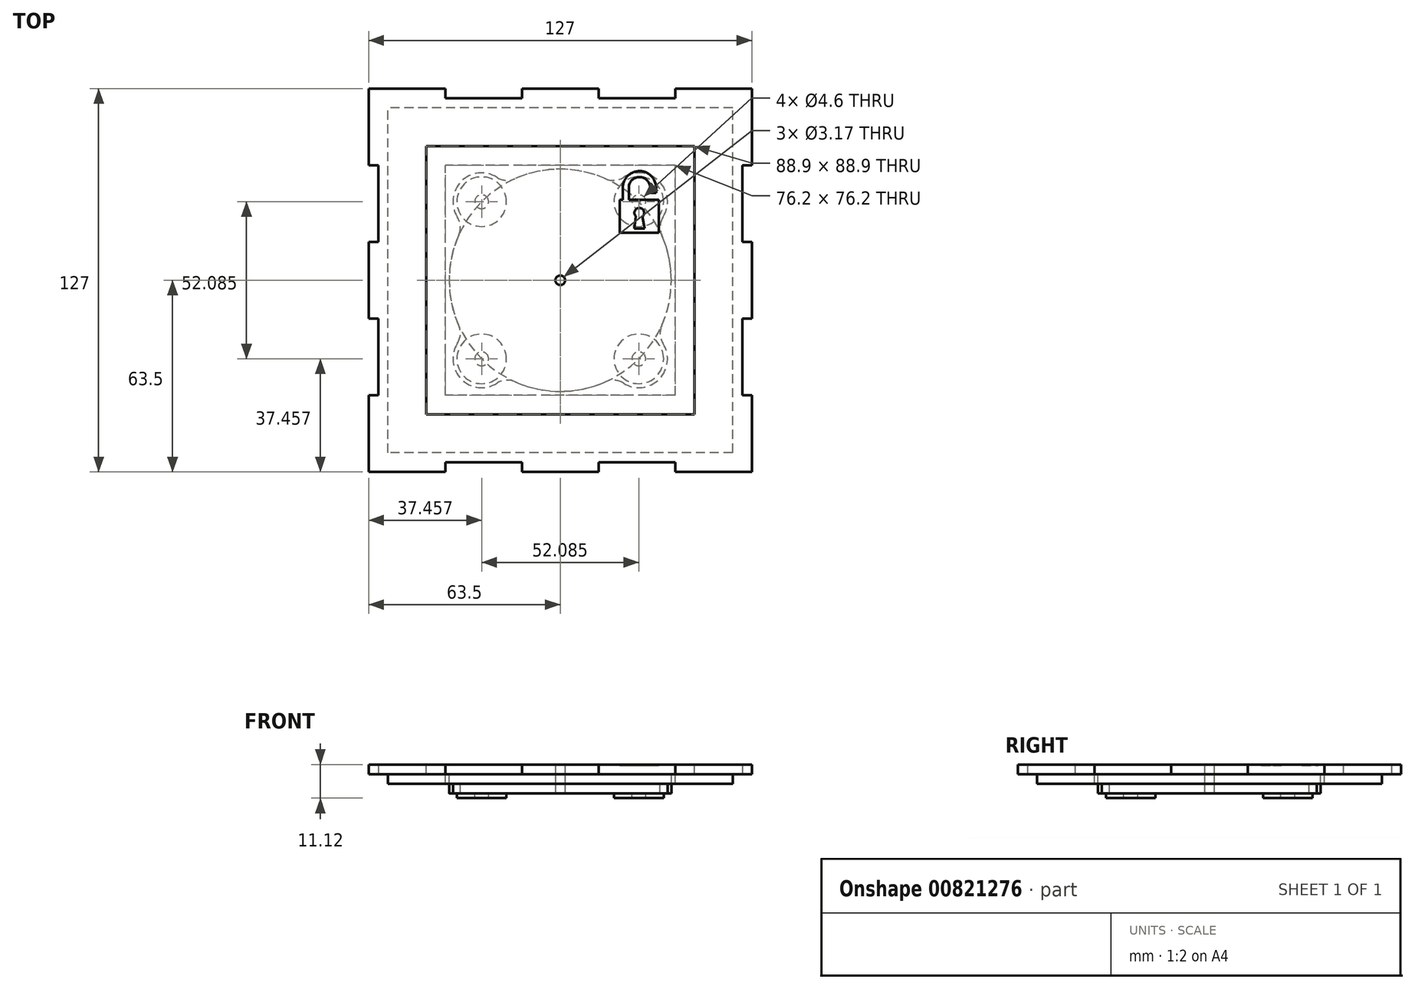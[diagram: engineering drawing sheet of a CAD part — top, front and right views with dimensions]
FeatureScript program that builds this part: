
annotation { "Feature Type Name" : "Feature", "Feature Type Description" : "" }
export const myFeature = defineFeature(function(context is Context, id is Id, definition is map)
    precondition{}
    {
        {
            var Q0;
            Q0=qCreatedBy(makeId("Top.planeOp"),FACE);
            var sketch = newSketch(context, id + "F0", { "sketchPlane" : qUnion([Q0])});
            skLineSegment(sketch, "E0.bottom", {"start": v(-63.5, 63.5) * mm, "end": v(63.5, 63.5) * mm});
            skLineSegment(sketch, "E0.top", {"start": v(-63.5, -63.5) * mm, "end": v(63.5, -63.5) * mm});
            skLineSegment(sketch, "E0.left", {"start": v(-63.5, 63.5) * mm, "end": v(-63.5, -63.5) * mm});
            skLineSegment(sketch, "E0.right", {"start": v(63.5, 63.5) * mm, "end": v(63.5, -63.5) * mm});
            skPoint(sketch, "E0.middle", {"position": v(0, 0) * mm});
            skLineSegment(sketch, "E1", {"start": v(-38.1, 63.5) * mm, "end": v(-38.1, -63.5) * mm});
            skLineSegment(sketch, "E2", {"start": v(-63.5, -38.1) * mm, "end": v(63.5, -38.1) * mm});
            skLineSegment(sketch, "E3.1.0.0", {"start": v(-12.7, 63.5) * mm, "end": v(-12.7, -63.5) * mm});
            skLineSegment(sketch, "E3.2.0.0", {"start": v(12.7, 63.5) * mm, "end": v(12.7, -63.5) * mm});
            skLineSegment(sketch, "E3.3.0.0", {"start": v(38.1, 63.5) * mm, "end": v(38.1, -63.5) * mm});
            skLineSegment(sketch, "E3.direction1", {"start": v(-38.1, -63.5) * mm, "end": v(-12.7, -63.5) * mm, "construction": true});
            skLineSegment(sketch, "E4.0.1.0", {"start": v(-63.5, -12.7) * mm, "end": v(63.5, -12.7) * mm});
            skLineSegment(sketch, "E4.0.2.0", {"start": v(-63.5, 12.7) * mm, "end": v(63.5, 12.7) * mm});
            skLineSegment(sketch, "E4.0.3.0", {"start": v(-63.5, 38.1) * mm, "end": v(63.5, 38.1) * mm});
            skLineSegment(sketch, "E4.1.0.0", {"start": v(-38.1, -38.1) * mm, "end": v(63.5, -38.1) * mm});
            skLineSegment(sketch, "E4.1.1.0", {"start": v(-38.1, -12.7) * mm, "end": v(63.5, -12.7) * mm});
            skLineSegment(sketch, "E4.1.2.0", {"start": v(-38.1, 12.7) * mm, "end": v(63.5, 12.7) * mm});
            skLineSegment(sketch, "E4.1.3.0", {"start": v(-38.1, 38.1) * mm, "end": v(63.5, 38.1) * mm});
            skLineSegment(sketch, "E4.2.0.0", {"start": v(-12.7, -38.1) * mm, "end": v(63.5, -38.1) * mm});
            skLineSegment(sketch, "E4.2.1.0", {"start": v(-12.7, -12.7) * mm, "end": v(63.5, -12.7) * mm});
            skLineSegment(sketch, "E4.2.2.0", {"start": v(-12.7, 12.7) * mm, "end": v(63.5, 12.7) * mm});
            skLineSegment(sketch, "E4.2.3.0", {"start": v(-12.7, 38.1) * mm, "end": v(63.5, 38.1) * mm});
            skLineSegment(sketch, "E4.direction1", {"start": v(-63.5, -38.1) * mm, "end": v(-38.1, -38.1) * mm, "construction": true});
            skLineSegment(sketch, "E4.direction2", {"start": v(-63.5, -38.1) * mm, "end": v(-63.5, -12.7) * mm, "construction": true});
            skLineSegment(sketch, "E5", {"start": v(-63.5, -60.33) * mm, "end": v(63.5, -60.32) * mm});
            skLineSegment(sketch, "E6", {"start": v(-60.33, 63.5) * mm, "end": v(-60.33, -63.5) * mm});
            skLineSegment(sketch, "E7", {"start": v(-63.5, 60.33) * mm, "end": v(63.5, 60.33) * mm});
            skLineSegment(sketch, "E8", {"start": v(60.32, 63.5) * mm, "end": v(60.32, -63.5) * mm});
            skSolve(sketch);
        }
        {
            var Q0;
            {var subQ0=sQuery(id+"F0.wireOp",EDGE,"E6");var subQ1=sQuery(id+"F0.wireOp",EDGE,"E0.bottom");var subQ2=makeQuery(id+"F0.imprint","INTERSECT",VERTEX,{"derivedFrom":[subQ1,subQ0]});Q0=makeQuery(id+"F0.imprint","IMPRINT",FACE,{"disambiguationData":[TD([[makeQuery(id+"F0.imprint","IMPRINT",EDGE,{"disambiguationData":[TD([[subQ2,1.0]])],"derivedFrom":subQ1}),-1.0]])]});}
            var Q1;
            {var subQ0=sQuery(id+"F0.wireOp",EDGE,"E0.right");var subQ1=sQuery(id+"F0.wireOp",EDGE,"E0.bottom");var subQ2=makeQuery(id+"F0.imprint","INTERSECT",VERTEX,{"derivedFrom":[subQ1,subQ0]});Q1=makeQuery(id+"F0.imprint","IMPRINT",FACE,{"disambiguationData":[TD([[makeQuery(id+"F0.imprint","IMPRINT",EDGE,{"disambiguationData":[TD([[subQ2,1.0]])],"derivedFrom":subQ1}),-1.0]])]});}
            var Q2;
            {var subQ0=sQuery(id+"F0.wireOp",EDGE,"E6");var subQ1=sQuery(id+"F0.wireOp",EDGE,"E0.top");var subQ2=makeQuery(id+"F0.imprint","INTERSECT",VERTEX,{"derivedFrom":[subQ1,subQ0]});Q2=makeQuery(id+"F0.imprint","IMPRINT",FACE,{"disambiguationData":[TD([[makeQuery(id+"F0.imprint","IMPRINT",EDGE,{"disambiguationData":[TD([[subQ2,1.0]])],"derivedFrom":subQ1}),1.0]])]});}
            var Q3;
            {var subQ0=sQuery(id+"F0.wireOp",EDGE,"E0.right");var subQ1=sQuery(id+"F0.wireOp",EDGE,"E0.top");var subQ2=makeQuery(id+"F0.imprint","INTERSECT",VERTEX,{"derivedFrom":[subQ1,subQ0]});Q3=makeQuery(id+"F0.imprint","IMPRINT",FACE,{"disambiguationData":[TD([[makeQuery(id+"F0.imprint","IMPRINT",EDGE,{"disambiguationData":[TD([[subQ2,1.0]])],"derivedFrom":subQ1}),1.0]])]});}
            var Q4;
            {var subQ0=sQuery(id+"F0.wireOp",EDGE,"E1");var subQ1=sQuery(id+"F0.wireOp",EDGE,"E0.bottom");var subQ2=makeQuery(id+"F0.imprint","INTERSECT",VERTEX,{"derivedFrom":[subQ1,subQ0]});Q4=makeQuery(id+"F0.imprint","IMPRINT",FACE,{"disambiguationData":[TD([[makeQuery(id+"F0.imprint","IMPRINT",EDGE,{"disambiguationData":[TD([[subQ2,1.0]])],"derivedFrom":subQ1}),-1.0]])]});}
            var Q5;
            {var subQ0=sQuery(id+"F0.wireOp",EDGE,"E3.1.0.0");var subQ1=sQuery(id+"F0.wireOp",EDGE,"E0.bottom");var subQ2=makeQuery(id+"F0.imprint","INTERSECT",VERTEX,{"derivedFrom":[subQ1,subQ0]});Q5=makeQuery(id+"F0.imprint","IMPRINT",FACE,{"disambiguationData":[TD([[makeQuery(id+"F0.imprint","IMPRINT",EDGE,{"disambiguationData":[TD([[subQ2,-1.0]])],"derivedFrom":subQ1}),-1.0]])]});}
            var Q6;
            {var subQ0=sQuery(id+"F0.wireOp",EDGE,"E3.3.0.0");var subQ1=sQuery(id+"F0.wireOp",EDGE,"E0.bottom");var subQ2=makeQuery(id+"F0.imprint","INTERSECT",VERTEX,{"derivedFrom":[subQ1,subQ0]});Q6=makeQuery(id+"F0.imprint","IMPRINT",FACE,{"disambiguationData":[TD([[makeQuery(id+"F0.imprint","IMPRINT",EDGE,{"disambiguationData":[TD([[subQ2,-1.0]])],"derivedFrom":subQ1}),-1.0]])]});}
            var Q7;
            {var subQ0=sQuery(id+"F0.wireOp",EDGE,"E1");var subQ1=sQuery(id+"F0.wireOp",EDGE,"E0.top");var subQ2=makeQuery(id+"F0.imprint","INTERSECT",VERTEX,{"derivedFrom":[subQ1,subQ0]});Q7=makeQuery(id+"F0.imprint","IMPRINT",FACE,{"disambiguationData":[TD([[makeQuery(id+"F0.imprint","IMPRINT",EDGE,{"disambiguationData":[TD([[subQ2,1.0]])],"derivedFrom":subQ1}),1.0]])]});}
            var Q8;
            {var subQ0=sQuery(id+"F0.wireOp",EDGE,"E3.1.0.0");var subQ1=sQuery(id+"F0.wireOp",EDGE,"E0.top");var subQ2=makeQuery(id+"F0.imprint","INTERSECT",VERTEX,{"derivedFrom":[subQ1,subQ0]});Q8=makeQuery(id+"F0.imprint","IMPRINT",FACE,{"disambiguationData":[TD([[makeQuery(id+"F0.imprint","IMPRINT",EDGE,{"disambiguationData":[TD([[subQ2,-1.0]])],"derivedFrom":subQ1}),1.0]])]});}
            var Q9;
            {var subQ0=sQuery(id+"F0.wireOp",EDGE,"E3.3.0.0");var subQ1=sQuery(id+"F0.wireOp",EDGE,"E0.top");var subQ2=makeQuery(id+"F0.imprint","INTERSECT",VERTEX,{"derivedFrom":[subQ1,subQ0]});Q9=makeQuery(id+"F0.imprint","IMPRINT",FACE,{"disambiguationData":[TD([[makeQuery(id+"F0.imprint","IMPRINT",EDGE,{"disambiguationData":[TD([[subQ2,-1.0]])],"derivedFrom":subQ1}),1.0]])]});}
            var Q10;
            {var subQ0=sQuery(id+"F0.wireOp",EDGE,"E7");var subQ1=sQuery(id+"F0.wireOp",EDGE,"E0.left");var subQ2=makeQuery(id+"F0.imprint","INTERSECT",VERTEX,{"derivedFrom":[subQ1,subQ0]});Q10=makeQuery(id+"F0.imprint","IMPRINT",FACE,{"disambiguationData":[TD([[makeQuery(id+"F0.imprint","IMPRINT",EDGE,{"disambiguationData":[TD([[subQ2,-1.0]])],"derivedFrom":subQ1}),1.0]])]});}
            var Q11;
            {var subQ0=sQuery(id+"F0.wireOp",EDGE,"E4.0.2.0");var subQ1=sQuery(id+"F0.wireOp",EDGE,"E0.left");var subQ2=makeQuery(id+"F0.imprint","INTERSECT",VERTEX,{"derivedFrom":[subQ1,subQ0]});Q11=makeQuery(id+"F0.imprint","IMPRINT",FACE,{"disambiguationData":[TD([[makeQuery(id+"F0.imprint","IMPRINT",EDGE,{"disambiguationData":[TD([[subQ2,-1.0]])],"derivedFrom":subQ1}),1.0]])]});}
            var Q12;
            {var subQ0=sQuery(id+"F0.wireOp",EDGE,"E2");var subQ1=sQuery(id+"F0.wireOp",EDGE,"E0.left");var subQ2=makeQuery(id+"F0.imprint","INTERSECT",VERTEX,{"derivedFrom":[subQ1,subQ0]});Q12=makeQuery(id+"F0.imprint","IMPRINT",FACE,{"disambiguationData":[TD([[makeQuery(id+"F0.imprint","IMPRINT",EDGE,{"disambiguationData":[TD([[subQ2,-1.0]])],"derivedFrom":subQ1}),1.0]])]});}
            var Q13;
            {var subQ0=sQuery(id+"F0.wireOp",EDGE,"E7");var subQ1=sQuery(id+"F0.wireOp",EDGE,"E0.right");var subQ2=makeQuery(id+"F0.imprint","INTERSECT",VERTEX,{"derivedFrom":[subQ1,subQ0]});Q13=makeQuery(id+"F0.imprint","IMPRINT",FACE,{"disambiguationData":[TD([[makeQuery(id+"F0.imprint","IMPRINT",EDGE,{"disambiguationData":[TD([[subQ2,-1.0]])],"derivedFrom":subQ1}),-1.0]])]});}
            var Q14;
            {var subQ0=sQuery(id+"F0.wireOp",EDGE,"E4.0.2.0");var subQ1=sQuery(id+"F0.wireOp",EDGE,"E0.right");var subQ2=makeQuery(id+"F0.imprint","INTERSECT",VERTEX,{"derivedFrom":[subQ1,subQ0]});Q14=makeQuery(id+"F0.imprint","IMPRINT",FACE,{"disambiguationData":[TD([[makeQuery(id+"F0.imprint","IMPRINT",EDGE,{"disambiguationData":[TD([[subQ2,-1.0]])],"derivedFrom":subQ1}),-1.0]])]});}
            var Q15;
            {var subQ0=sQuery(id+"F0.wireOp",EDGE,"E5");var subQ1=sQuery(id+"F0.wireOp",EDGE,"E0.right");var subQ2=makeQuery(id+"F0.imprint","INTERSECT",VERTEX,{"derivedFrom":[subQ1,subQ0]});Q15=makeQuery(id+"F0.imprint","IMPRINT",FACE,{"disambiguationData":[TD([[makeQuery(id+"F0.imprint","IMPRINT",EDGE,{"disambiguationData":[TD([[subQ2,1.0]])],"derivedFrom":subQ1}),-1.0]])]});}
            var Q16;
            {var subQ0=sQuery(id+"F0.wireOp",EDGE,"E7");var subQ1=sQuery(id+"F0.wireOp",EDGE,"E1");var subQ2=makeQuery(id+"F0.imprint","INTERSECT",VERTEX,{"derivedFrom":[subQ1,subQ0]});Q16=makeQuery(id+"F0.imprint","IMPRINT",FACE,{"disambiguationData":[TD([[makeQuery(id+"F0.imprint","IMPRINT",EDGE,{"disambiguationData":[TD([[subQ2,-1.0]])],"derivedFrom":subQ1}),-1.0]])]});}
            var Q17;
            {var subQ0=sQuery(id+"F0.wireOp",EDGE,"E7");var subQ1=sQuery(id+"F0.wireOp",EDGE,"E1");var subQ2=makeQuery(id+"F0.imprint","INTERSECT",VERTEX,{"derivedFrom":[subQ1,subQ0]});Q17=makeQuery(id+"F0.imprint","IMPRINT",FACE,{"disambiguationData":[TD([[makeQuery(id+"F0.imprint","IMPRINT",EDGE,{"disambiguationData":[TD([[subQ2,-1.0]])],"derivedFrom":subQ1}),1.0]])]});}
            var Q18;
            {var subQ0=sQuery(id+"F0.wireOp",EDGE,"E7");var subQ1=sQuery(id+"F0.wireOp",EDGE,"E3.2.0.0");var subQ2=makeQuery(id+"F0.imprint","INTERSECT",VERTEX,{"derivedFrom":[subQ1,subQ0]});Q18=makeQuery(id+"F0.imprint","IMPRINT",FACE,{"disambiguationData":[TD([[makeQuery(id+"F0.imprint","IMPRINT",EDGE,{"disambiguationData":[TD([[subQ2,-1.0]])],"derivedFrom":subQ1}),1.0]])]});}
            var Q19;
            {var subQ0=sQuery(id+"F0.wireOp",EDGE,"E7");var subQ1=sQuery(id+"F0.wireOp",EDGE,"E3.3.0.0");var subQ2=makeQuery(id+"F0.imprint","INTERSECT",VERTEX,{"derivedFrom":[subQ1,subQ0]});Q19=makeQuery(id+"F0.imprint","IMPRINT",FACE,{"disambiguationData":[TD([[makeQuery(id+"F0.imprint","IMPRINT",EDGE,{"disambiguationData":[TD([[subQ2,-1.0]])],"derivedFrom":subQ1}),1.0]])]});}
            var Q20;
            {var subQ0=sQuery(id+"F0.wireOp",EDGE,"E4.0.2.0");var subQ1=sQuery(id+"F0.wireOp",EDGE,"E3.3.0.0");var subQ2=makeQuery(id+"F0.imprint","INTERSECT",VERTEX,{"derivedFrom":[subQ1,subQ0]});Q20=makeQuery(id+"F0.imprint","IMPRINT",FACE,{"disambiguationData":[TD([[makeQuery(id+"F0.imprint","IMPRINT",EDGE,{"disambiguationData":[TD([[subQ2,1.0]])],"derivedFrom":subQ1}),1.0]])]});}
            var Q21;
            {var subQ0=sQuery(id+"F0.wireOp",EDGE,"E4.0.2.0");var subQ1=sQuery(id+"F0.wireOp",EDGE,"E3.2.0.0");var subQ2=makeQuery(id+"F0.imprint","INTERSECT",VERTEX,{"derivedFrom":[subQ1,subQ0]});Q21=makeQuery(id+"F0.imprint","IMPRINT",FACE,{"disambiguationData":[TD([[makeQuery(id+"F0.imprint","IMPRINT",EDGE,{"disambiguationData":[TD([[subQ2,1.0]])],"derivedFrom":subQ1}),1.0]])]});}
            var Q22;
            {var subQ0=sQuery(id+"F0.wireOp",EDGE,"E4.0.2.0");var subQ1=sQuery(id+"F0.wireOp",EDGE,"E3.1.0.0");var subQ2=makeQuery(id+"F0.imprint","INTERSECT",VERTEX,{"derivedFrom":[subQ1,subQ0]});Q22=makeQuery(id+"F0.imprint","IMPRINT",FACE,{"disambiguationData":[TD([[makeQuery(id+"F0.imprint","IMPRINT",EDGE,{"disambiguationData":[TD([[subQ2,1.0]])],"derivedFrom":subQ1}),1.0]])]});}
            var Q23;
            {var subQ0=sQuery(id+"F0.wireOp",EDGE,"E4.0.2.0");var subQ1=sQuery(id+"F0.wireOp",EDGE,"E1");var subQ2=makeQuery(id+"F0.imprint","INTERSECT",VERTEX,{"derivedFrom":[subQ1,subQ0]});Q23=makeQuery(id+"F0.imprint","IMPRINT",FACE,{"disambiguationData":[TD([[makeQuery(id+"F0.imprint","IMPRINT",EDGE,{"disambiguationData":[TD([[subQ2,1.0]])],"derivedFrom":subQ1}),1.0]])]});}
            var Q24;
            {var subQ0=sQuery(id+"F0.wireOp",EDGE,"E4.0.2.0");var subQ1=sQuery(id+"F0.wireOp",EDGE,"E1");var subQ2=makeQuery(id+"F0.imprint","INTERSECT",VERTEX,{"derivedFrom":[subQ1,subQ0]});Q24=makeQuery(id+"F0.imprint","IMPRINT",FACE,{"disambiguationData":[TD([[makeQuery(id+"F0.imprint","IMPRINT",EDGE,{"disambiguationData":[TD([[subQ2,1.0]])],"derivedFrom":subQ1}),-1.0]])]});}
            var Q25;
            {var subQ0=sQuery(id+"F0.wireOp",EDGE,"E4.0.2.0");var subQ1=sQuery(id+"F0.wireOp",EDGE,"E1");var subQ2=makeQuery(id+"F0.imprint","INTERSECT",VERTEX,{"derivedFrom":[subQ1,subQ0]});Q25=makeQuery(id+"F0.imprint","IMPRINT",FACE,{"disambiguationData":[TD([[makeQuery(id+"F0.imprint","IMPRINT",EDGE,{"disambiguationData":[TD([[subQ2,-1.0]])],"derivedFrom":subQ1}),-1.0]])]});}
            var Q26;
            {var subQ0=sQuery(id+"F0.wireOp",EDGE,"E4.0.2.0");var subQ1=sQuery(id+"F0.wireOp",EDGE,"E1");var subQ2=makeQuery(id+"F0.imprint","INTERSECT",VERTEX,{"derivedFrom":[subQ1,subQ0]});Q26=makeQuery(id+"F0.imprint","IMPRINT",FACE,{"disambiguationData":[TD([[makeQuery(id+"F0.imprint","IMPRINT",EDGE,{"disambiguationData":[TD([[subQ2,-1.0]])],"derivedFrom":subQ1}),1.0]])]});}
            var Q27;
            {var subQ0=sQuery(id+"F0.wireOp",EDGE,"E4.0.1.0");var subQ1=sQuery(id+"F0.wireOp",EDGE,"E3.1.0.0");var subQ2=makeQuery(id+"F0.imprint","INTERSECT",VERTEX,{"derivedFrom":[subQ1,subQ0]});Q27=makeQuery(id+"F0.imprint","IMPRINT",FACE,{"disambiguationData":[TD([[makeQuery(id+"F0.imprint","IMPRINT",EDGE,{"disambiguationData":[TD([[subQ2,1.0]])],"derivedFrom":subQ1}),1.0]])]});}
            var Q28;
            {var subQ0=sQuery(id+"F0.wireOp",EDGE,"E4.0.1.0");var subQ1=sQuery(id+"F0.wireOp",EDGE,"E3.2.0.0");var subQ2=makeQuery(id+"F0.imprint","INTERSECT",VERTEX,{"derivedFrom":[subQ1,subQ0]});Q28=makeQuery(id+"F0.imprint","IMPRINT",FACE,{"disambiguationData":[TD([[makeQuery(id+"F0.imprint","IMPRINT",EDGE,{"disambiguationData":[TD([[subQ2,1.0]])],"derivedFrom":subQ1}),1.0]])]});}
            var Q29;
            {var subQ0=sQuery(id+"F0.wireOp",EDGE,"E4.0.1.0");var subQ1=sQuery(id+"F0.wireOp",EDGE,"E3.3.0.0");var subQ2=makeQuery(id+"F0.imprint","INTERSECT",VERTEX,{"derivedFrom":[subQ1,subQ0]});Q29=makeQuery(id+"F0.imprint","IMPRINT",FACE,{"disambiguationData":[TD([[makeQuery(id+"F0.imprint","IMPRINT",EDGE,{"disambiguationData":[TD([[subQ2,1.0]])],"derivedFrom":subQ1}),1.0]])]});}
            var Q30;
            {var subQ0=sQuery(id+"F0.wireOp",EDGE,"E3.3.0.0");var subQ1=sQuery(id+"F0.wireOp",EDGE,"E2");var subQ2=makeQuery(id+"F0.imprint","INTERSECT",VERTEX,{"derivedFrom":[subQ1,subQ0]});Q30=makeQuery(id+"F0.imprint","IMPRINT",FACE,{"disambiguationData":[TD([[makeQuery(id+"F0.imprint","IMPRINT",EDGE,{"disambiguationData":[TD([[subQ2,-1.0]])],"derivedFrom":subQ1}),1.0]])]});}
            var Q31;
            {var subQ0=sQuery(id+"F0.wireOp",EDGE,"E3.2.0.0");var subQ1=sQuery(id+"F0.wireOp",EDGE,"E2");var subQ2=makeQuery(id+"F0.imprint","INTERSECT",VERTEX,{"derivedFrom":[subQ1,subQ0]});Q31=makeQuery(id+"F0.imprint","IMPRINT",FACE,{"disambiguationData":[TD([[makeQuery(id+"F0.imprint","IMPRINT",EDGE,{"disambiguationData":[TD([[subQ2,-1.0]])],"derivedFrom":subQ1}),1.0]])]});}
            var Q32;
            {var subQ0=sQuery(id+"F0.wireOp",EDGE,"E3.1.0.0");var subQ1=sQuery(id+"F0.wireOp",EDGE,"E2");var subQ2=makeQuery(id+"F0.imprint","INTERSECT",VERTEX,{"derivedFrom":[subQ1,subQ0]});Q32=makeQuery(id+"F0.imprint","IMPRINT",FACE,{"disambiguationData":[TD([[makeQuery(id+"F0.imprint","IMPRINT",EDGE,{"disambiguationData":[TD([[subQ2,-1.0]])],"derivedFrom":subQ1}),1.0]])]});}
            var Q33;
            {var subQ0=sQuery(id+"F0.wireOp",EDGE,"E4.0.1.0");var subQ1=sQuery(id+"F0.wireOp",EDGE,"E1");var subQ2=makeQuery(id+"F0.imprint","INTERSECT",VERTEX,{"derivedFrom":[subQ1,subQ0]});Q33=makeQuery(id+"F0.imprint","IMPRINT",FACE,{"disambiguationData":[TD([[makeQuery(id+"F0.imprint","IMPRINT",EDGE,{"disambiguationData":[TD([[subQ2,-1.0]])],"derivedFrom":subQ1}),1.0]])]});}
            var Q34;
            {var subQ0=sQuery(id+"F0.wireOp",EDGE,"E4.0.1.0");var subQ1=sQuery(id+"F0.wireOp",EDGE,"E1");var subQ2=makeQuery(id+"F0.imprint","INTERSECT",VERTEX,{"derivedFrom":[subQ1,subQ0]});Q34=makeQuery(id+"F0.imprint","IMPRINT",FACE,{"disambiguationData":[TD([[makeQuery(id+"F0.imprint","IMPRINT",EDGE,{"disambiguationData":[TD([[subQ2,-1.0]])],"derivedFrom":subQ1}),-1.0]])]});}
            var Q35;
            {var subQ0=sQuery(id+"F0.wireOp",EDGE,"E5");var subQ1=sQuery(id+"F0.wireOp",EDGE,"E1");var subQ2=makeQuery(id+"F0.imprint","INTERSECT",VERTEX,{"derivedFrom":[subQ1,subQ0]});Q35=makeQuery(id+"F0.imprint","IMPRINT",FACE,{"disambiguationData":[TD([[makeQuery(id+"F0.imprint","IMPRINT",EDGE,{"disambiguationData":[TD([[subQ2,1.0]])],"derivedFrom":subQ1}),-1.0]])]});}
            var Q36;
            {var subQ0=sQuery(id+"F0.wireOp",EDGE,"E5");var subQ1=sQuery(id+"F0.wireOp",EDGE,"E1");var subQ2=makeQuery(id+"F0.imprint","INTERSECT",VERTEX,{"derivedFrom":[subQ1,subQ0]});Q36=makeQuery(id+"F0.imprint","IMPRINT",FACE,{"disambiguationData":[TD([[makeQuery(id+"F0.imprint","IMPRINT",EDGE,{"disambiguationData":[TD([[subQ2,1.0]])],"derivedFrom":subQ1}),1.0]])]});}
            var Q37;
            {var subQ0=sQuery(id+"F0.wireOp",EDGE,"E3.2.0.0");var subQ1=sQuery(id+"F0.wireOp",EDGE,"E2");var subQ2=makeQuery(id+"F0.imprint","INTERSECT",VERTEX,{"derivedFrom":[subQ1,subQ0]});Q37=makeQuery(id+"F0.imprint","IMPRINT",FACE,{"disambiguationData":[TD([[makeQuery(id+"F0.imprint","IMPRINT",EDGE,{"disambiguationData":[TD([[subQ2,-1.0]])],"derivedFrom":subQ1}),-1.0]])]});}
            var Q38;
            {var subQ0=sQuery(id+"F0.wireOp",EDGE,"E3.3.0.0");var subQ1=sQuery(id+"F0.wireOp",EDGE,"E2");var subQ2=makeQuery(id+"F0.imprint","INTERSECT",VERTEX,{"derivedFrom":[subQ1,subQ0]});Q38=makeQuery(id+"F0.imprint","IMPRINT",FACE,{"disambiguationData":[TD([[makeQuery(id+"F0.imprint","IMPRINT",EDGE,{"disambiguationData":[TD([[subQ2,-1.0]])],"derivedFrom":subQ1}),-1.0]])]});}
            var Q39;
            {var subQ0=sQuery(id+"F0.wireOp",EDGE,"E7");var subQ1=sQuery(id+"F0.wireOp",EDGE,"E3.1.0.0");var subQ2=makeQuery(id+"F0.imprint","INTERSECT",VERTEX,{"derivedFrom":[subQ1,subQ0]});Q39=makeQuery(id+"F0.imprint","IMPRINT",FACE,{"disambiguationData":[TD([[makeQuery(id+"F0.imprint","IMPRINT",EDGE,{"disambiguationData":[TD([[subQ2,-1.0]])],"derivedFrom":subQ1}),1.0]])]});}
            var Q40;
            {var subQ0=sQuery(id+"F0.wireOp",EDGE,"E3.1.0.0");var subQ1=sQuery(id+"F0.wireOp",EDGE,"E2");var subQ2=makeQuery(id+"F0.imprint","INTERSECT",VERTEX,{"derivedFrom":[subQ1,subQ0]});Q40=makeQuery(id+"F0.imprint","IMPRINT",FACE,{"disambiguationData":[TD([[makeQuery(id+"F0.imprint","IMPRINT",EDGE,{"disambiguationData":[TD([[subQ2,-1.0]])],"derivedFrom":subQ1}),-1.0]])]});}
            extrude(context, id + "F1", {"entities" : qUnion([Q0, Q1, Q2, Q3, Q4, Q5, Q6, Q7, Q8, Q9, Q10, Q11, Q12, Q13, Q14, Q15, Q16, Q17, Q18, Q19, Q20, Q21, Q22, Q23, Q24, Q25, Q26, Q27, Q28, Q29, Q30, Q31, Q32, Q33, Q34, Q35, Q36, Q37, Q38, Q39, Q40]), "depth" : 3.17 * mm, "offsetDistance" : 25.4 * mm});
        }
        {
            var Q0;
            Q0=makeQuery(id+"F1.opExtrude","CAP_FACE",FACE,{"disambiguationData":[OSD([sQuery(id+"F0.wireOp",EDGE,"E0.bottom"),sQuery(id+"F0.wireOp",EDGE,"E0.top"),sQuery(id+"F0.wireOp",EDGE,"E0.left"),sQuery(id+"F0.wireOp",EDGE,"E0.right"),sQuery(id+"F0.wireOp",EDGE,"E1"),sQuery(id+"F0.wireOp",EDGE,"E2"),sQuery(id+"F0.wireOp",EDGE,"E3.1.0.0"),sQuery(id+"F0.wireOp",EDGE,"E3.2.0.0"),sQuery(id+"F0.wireOp",EDGE,"E3.3.0.0"),sQuery(id+"F0.wireOp",EDGE,"E4.0.1.0"),sQuery(id+"F0.wireOp",EDGE,"E4.0.2.0"),sQuery(id+"F0.wireOp",EDGE,"E4.0.3.0"),sQuery(id+"F0.wireOp",EDGE,"E5"),sQuery(id+"F0.wireOp",EDGE,"E6"),sQuery(id+"F0.wireOp",EDGE,"E7"),sQuery(id+"F0.wireOp",EDGE,"E8")])],"isStart":false});
            var sketch = newSketch(context, id + "F2", { "sketchPlane" : qUnion([Q0])});
            skLineSegment(sketch, "E9.bottom", {"start": v(44.45, 44.45) * mm, "end": v(-44.45, 44.45) * mm});
            skLineSegment(sketch, "E9.top", {"start": v(44.45, -44.45) * mm, "end": v(-44.45, -44.45) * mm});
            skLineSegment(sketch, "E9.left", {"start": v(44.45, 44.45) * mm, "end": v(44.45, -44.45) * mm});
            skLineSegment(sketch, "E9.right", {"start": v(-44.45, 44.45) * mm, "end": v(-44.45, -44.45) * mm});
            skPoint(sketch, "E9.middle", {"position": v(0, 0) * mm});
            skSolve(sketch);
        }
        {
            var Q0;
            Q0 = qSketchRegion(id + "F2", true);
            extrude(context, id + "F3", {"entities" : qUnion([Q0]), "operationType" : NewBodyOperationType.REMOVE, "oppositeDirection" : true, "depth" : 25.4 * mm, "offsetDistance" : 25.4 * mm});
        }
        {
            var Q0;
            Q0=qCreatedBy(makeId("Top.planeOp"),FACE);
            var sketch = newSketch(context, id + "F4", { "sketchPlane" : qUnion([Q0])});
            skLineSegment(sketch, "E10.bottom", {"start": v(-44.45, 44.45) * mm, "end": v(44.45, 44.45) * mm});
            skLineSegment(sketch, "E10.top", {"start": v(-44.45, -44.45) * mm, "end": v(44.45, -44.45) * mm});
            skLineSegment(sketch, "E10.left", {"start": v(-44.45, 44.45) * mm, "end": v(-44.45, -44.45) * mm});
            skLineSegment(sketch, "E10.right", {"start": v(44.45, 44.45) * mm, "end": v(44.45, -44.45) * mm});
            skPoint(sketch, "E10.middle", {"position": v(0, 0) * mm});
            skSolve(sketch);
        }
        {
            var Q0;
            Q0 = qSketchRegion(id + "F4", true);
            extrude(context, id + "F5", {"entities" : qUnion([Q0]), "depth" : 3.17 * mm, "offsetDistance" : 25.4 * mm});
        }
        {
            var Q0;
            Q0=makeQuery(id+"F1.opExtrude","CAP_FACE",FACE,{"disambiguationData":[OSD([sQuery(id+"F0.wireOp",EDGE,"E0.bottom"),sQuery(id+"F0.wireOp",EDGE,"E0.top"),sQuery(id+"F0.wireOp",EDGE,"E0.left"),sQuery(id+"F0.wireOp",EDGE,"E0.right"),sQuery(id+"F0.wireOp",EDGE,"E1"),sQuery(id+"F0.wireOp",EDGE,"E2"),sQuery(id+"F0.wireOp",EDGE,"E3.1.0.0"),sQuery(id+"F0.wireOp",EDGE,"E3.2.0.0"),sQuery(id+"F0.wireOp",EDGE,"E3.3.0.0"),sQuery(id+"F0.wireOp",EDGE,"E4.0.1.0"),sQuery(id+"F0.wireOp",EDGE,"E4.0.2.0"),sQuery(id+"F0.wireOp",EDGE,"E4.0.3.0"),sQuery(id+"F0.wireOp",EDGE,"E5"),sQuery(id+"F0.wireOp",EDGE,"E6"),sQuery(id+"F0.wireOp",EDGE,"E7"),sQuery(id+"F0.wireOp",EDGE,"E8")])],"isStart":true});
            var sketch = newSketch(context, id + "F6", { "sketchPlane" : qUnion([Q0])});
            skLineSegment(sketch, "E11.bottom", {"start": v(57.15, 57.15) * mm, "end": v(-57.15, 57.15) * mm});
            skLineSegment(sketch, "E11.top", {"start": v(57.15, -57.15) * mm, "end": v(-57.15, -57.15) * mm});
            skLineSegment(sketch, "E11.left", {"start": v(57.15, 57.15) * mm, "end": v(57.15, -57.15) * mm});
            skLineSegment(sketch, "E11.right", {"start": v(-57.15, 57.15) * mm, "end": v(-57.15, -57.15) * mm});
            skPoint(sketch, "E11.middle", {"position": v(0, 0) * mm});
            skLineSegment(sketch, "E12.bottom", {"start": v(38.1, 38.1) * mm, "end": v(-38.1, 38.1) * mm});
            skLineSegment(sketch, "E12.top", {"start": v(38.1, -38.1) * mm, "end": v(-38.1, -38.1) * mm});
            skLineSegment(sketch, "E12.left", {"start": v(38.1, 38.1) * mm, "end": v(38.1, -38.1) * mm});
            skLineSegment(sketch, "E12.right", {"start": v(-38.1, 38.1) * mm, "end": v(-38.1, -38.1) * mm});
            skSolve(sketch);
        }
        {
            var Q0;
            Q0 = qSketchRegion(id + "F6", true);
            extrude(context, id + "F7", {"entities" : qUnion([Q0]), "depth" : 3.17 * mm, "offsetDistance" : 25.4 * mm});
        }
        {
            var Q0;
            Q0=makeQuery(id+"F5.opExtrude","CAP_FACE",FACE,{"disambiguationData":[OSD([sQuery(id+"F4.wireOp",EDGE,"E10.bottom"),sQuery(id+"F4.wireOp",EDGE,"E10.top"),sQuery(id+"F4.wireOp",EDGE,"E10.left"),sQuery(id+"F4.wireOp",EDGE,"E10.right")])],"isStart":true});
            var sketch = newSketch(context, id + "F8", { "sketchPlane" : qUnion([Q0])});
            skCircle(sketch, "E13", {"center": v(0, 0) * mm, "radius": 36.83 * mm});
            skSolve(sketch);
        }
        {
            var Q0;
            Q0 = qSketchRegion(id + "F8", true);
            extrude(context, id + "F9", {"entities" : qUnion([Q0]), "depth" : 3.17 * mm, "offsetDistance" : 25.4 * mm});
        }
        {
            var Q0;
            Q0=makeQuery(id+"F9.opExtrude","CAP_FACE",FACE,{"disambiguationData":[OSD([sQuery(id+"F8.wireOp",EDGE,"E13")])],"isStart":false});
            var sketch = newSketch(context, id + "F10", { "sketchPlane" : qUnion([Q0])});
            skCircle(sketch, "E14", {"center": v(0, 0) * mm, "radius": 36.83 * mm});
            skLineSegment(sketch, "E15", {"start": v(0, 0) * mm, "end": v(-38.1, 38.1) * mm});
            skCircle(sketch, "E16", {"center": v(-26.04, 26.04) * mm, "radius": 9.53 * mm});
            skCircle(sketch, "E17", {"center": v(-39.45, 17.55) * mm, "radius": 6.35 * mm});
            skCircle(sketch, "E18.MirrorC", {"center": v(-17.55, 39.45) * mm, "radius": 6.35 * mm});
            skCircle(sketch, "E19.1.0", {"center": v(-26.04, -26.04) * mm, "radius": 9.53 * mm});
            skCircle(sketch, "E19.1.1", {"center": v(-39.45, -17.55) * mm, "radius": 6.35 * mm});
            skCircle(sketch, "E19.1.2", {"center": v(-17.55, -39.45) * mm, "radius": 6.35 * mm});
            skCircle(sketch, "E19.2.0", {"center": v(26.04, -26.04) * mm, "radius": 9.53 * mm});
            skCircle(sketch, "E19.2.1", {"center": v(17.55, -39.45) * mm, "radius": 6.35 * mm});
            skCircle(sketch, "E19.2.2", {"center": v(39.45, -17.55) * mm, "radius": 6.35 * mm});
            skCircle(sketch, "E19.3.0", {"center": v(26.04, 26.04) * mm, "radius": 9.53 * mm});
            skCircle(sketch, "E19.3.1", {"center": v(39.45, 17.55) * mm, "radius": 6.35 * mm});
            skCircle(sketch, "E19.3.2", {"center": v(17.55, 39.45) * mm, "radius": 6.35 * mm});
            skSolve(sketch);
        }
        {
            var Q0;
            {var subQ0=sQuery(id+"F10.wireOp",EDGE,"E14");var subQ10=makeQuery(id+"F10.imprint","INTERSECT",VERTEX,{"derivedFrom":[subQ0,sQuery(id+"F10.wireOp",EDGE,"E19.3.1")]});Q0=makeQuery(id+"F10.imprint","IMPRINT",FACE,{"disambiguationData":[TD([[makeQuery(id+"F10.imprint","IMPRINT",EDGE,{"disambiguationData":[TD([[subQ10,-1.0]])],"derivedFrom":subQ0}),1.0]])]});}
            var Q1;
            {var subQ0=sQuery(id+"F10.wireOp",EDGE,"E16");var subQ1=sQuery(id+"F10.wireOp",EDGE,"E14");var subQ2=makeQuery(id+"F10.imprint","INTERSECT",VERTEX,{"disambiguationData":[OD(0.0)],"derivedFrom":[subQ1,subQ0]});Q1=makeQuery(id+"F10.imprint","IMPRINT",FACE,{"disambiguationData":[TD([[makeQuery(id+"F10.imprint","IMPRINT",EDGE,{"disambiguationData":[TD([[subQ2,-1.0]])],"derivedFrom":subQ1}),1.0]])]});}
            var Q2;
            {var subQ0=sQuery(id+"F10.wireOp",EDGE,"E15");var subQ1=sQuery(id+"F10.wireOp",EDGE,"E14");var subQ2=makeQuery(id+"F10.imprint","INTERSECT",VERTEX,{"derivedFrom":[subQ1,subQ0]});Q2=makeQuery(id+"F10.imprint","IMPRINT",FACE,{"disambiguationData":[TD([[makeQuery(id+"F10.imprint","IMPRINT",EDGE,{"disambiguationData":[TD([[subQ2,-1.0]])],"derivedFrom":subQ1}),1.0]])]});}
            var Q3;
            {var subQ0=sQuery(id+"F10.wireOp",EDGE,"E19.1.0");var subQ1=sQuery(id+"F10.wireOp",EDGE,"E14");var subQ2=makeQuery(id+"F10.imprint","INTERSECT",VERTEX,{"disambiguationData":[OD(0.0)],"derivedFrom":[subQ1,subQ0]});Q3=makeQuery(id+"F10.imprint","IMPRINT",FACE,{"disambiguationData":[TD([[makeQuery(id+"F10.imprint","IMPRINT",EDGE,{"disambiguationData":[TD([[subQ2,-1.0]])],"derivedFrom":subQ1}),1.0]])]});}
            var Q4;
            {var subQ0=sQuery(id+"F10.wireOp",EDGE,"E19.2.0");var subQ1=sQuery(id+"F10.wireOp",EDGE,"E14");var subQ2=makeQuery(id+"F10.imprint","INTERSECT",VERTEX,{"disambiguationData":[OD(0.0)],"derivedFrom":[subQ1,subQ0]});Q4=makeQuery(id+"F10.imprint","IMPRINT",FACE,{"disambiguationData":[TD([[makeQuery(id+"F10.imprint","IMPRINT",EDGE,{"disambiguationData":[TD([[subQ2,-1.0]])],"derivedFrom":subQ1}),1.0]])]});}
            var Q5;
            {var subQ0=sQuery(id+"F10.wireOp",EDGE,"E19.3.0");var subQ1=sQuery(id+"F10.wireOp",EDGE,"E14");var subQ2=makeQuery(id+"F10.imprint","INTERSECT",VERTEX,{"disambiguationData":[OD(0.0)],"derivedFrom":[subQ1,subQ0]});Q5=makeQuery(id+"F10.imprint","IMPRINT",FACE,{"disambiguationData":[TD([[makeQuery(id+"F10.imprint","IMPRINT",EDGE,{"disambiguationData":[TD([[subQ2,-1.0]])],"derivedFrom":subQ1}),1.0]])]});}
            var Q6;
            {var subQ0=sQuery(id+"F10.wireOp",EDGE,"E19.3.0");var subQ1=sQuery(id+"F10.wireOp",EDGE,"E14");var subQ2=makeQuery(id+"F10.imprint","INTERSECT",VERTEX,{"disambiguationData":[OD(0.0)],"derivedFrom":[subQ1,subQ0]});Q6=makeQuery(id+"F10.imprint","IMPRINT",FACE,{"disambiguationData":[TD([[makeQuery(id+"F10.imprint","IMPRINT",EDGE,{"disambiguationData":[TD([[subQ2,-1.0]])],"derivedFrom":subQ1}),-1.0]])]});}
            var Q7;
            {var subQ0=sQuery(id+"F10.wireOp",EDGE,"E15");var subQ1=sQuery(id+"F10.wireOp",EDGE,"E14");var subQ2=makeQuery(id+"F10.imprint","INTERSECT",VERTEX,{"derivedFrom":[subQ1,subQ0]});Q7=makeQuery(id+"F10.imprint","IMPRINT",FACE,{"disambiguationData":[TD([[makeQuery(id+"F10.imprint","IMPRINT",EDGE,{"disambiguationData":[TD([[subQ2,-1.0]])],"derivedFrom":subQ1}),-1.0]])]});}
            var Q8;
            {var subQ0=sQuery(id+"F10.wireOp",EDGE,"E16");var subQ1=sQuery(id+"F10.wireOp",EDGE,"E14");var subQ2=makeQuery(id+"F10.imprint","INTERSECT",VERTEX,{"disambiguationData":[OD(0.0)],"derivedFrom":[subQ1,subQ0]});Q8=makeQuery(id+"F10.imprint","IMPRINT",FACE,{"disambiguationData":[TD([[makeQuery(id+"F10.imprint","IMPRINT",EDGE,{"disambiguationData":[TD([[subQ2,-1.0]])],"derivedFrom":subQ1}),-1.0]])]});}
            var Q9;
            {var subQ0=sQuery(id+"F10.wireOp",EDGE,"E19.1.0");var subQ1=sQuery(id+"F10.wireOp",EDGE,"E14");var subQ2=makeQuery(id+"F10.imprint","INTERSECT",VERTEX,{"disambiguationData":[OD(0.0)],"derivedFrom":[subQ1,subQ0]});Q9=makeQuery(id+"F10.imprint","IMPRINT",FACE,{"disambiguationData":[TD([[makeQuery(id+"F10.imprint","IMPRINT",EDGE,{"disambiguationData":[TD([[subQ2,-1.0]])],"derivedFrom":subQ1}),-1.0]])]});}
            var Q10;
            {var subQ0=sQuery(id+"F10.wireOp",EDGE,"E19.2.0");var subQ1=sQuery(id+"F10.wireOp",EDGE,"E14");var subQ2=makeQuery(id+"F10.imprint","INTERSECT",VERTEX,{"disambiguationData":[OD(0.0)],"derivedFrom":[subQ1,subQ0]});Q10=makeQuery(id+"F10.imprint","IMPRINT",FACE,{"disambiguationData":[TD([[makeQuery(id+"F10.imprint","IMPRINT",EDGE,{"disambiguationData":[TD([[subQ2,-1.0]])],"derivedFrom":subQ1}),-1.0]])]});}
            var Q11;
            {var subQ0=sQuery(id+"F10.wireOp",EDGE,"E19.3.1");var subQ1=sQuery(id+"F10.wireOp",EDGE,"E14");var subQ2=makeQuery(id+"F10.imprint","INTERSECT",VERTEX,{"derivedFrom":[subQ1,subQ0]});Q11=makeQuery(id+"F10.imprint","IMPRINT",FACE,{"disambiguationData":[TD([[makeQuery(id+"F10.imprint","IMPRINT",EDGE,{"disambiguationData":[TD([[subQ2,-1.0]])],"derivedFrom":subQ1}),-1.0]])]});}
            var Q12;
            {var subQ0=sQuery(id+"F10.wireOp",EDGE,"E19.3.2");var subQ1=sQuery(id+"F10.wireOp",EDGE,"E14");var subQ2=makeQuery(id+"F10.imprint","INTERSECT",VERTEX,{"derivedFrom":[subQ1,subQ0]});Q12=makeQuery(id+"F10.imprint","IMPRINT",FACE,{"disambiguationData":[TD([[makeQuery(id+"F10.imprint","IMPRINT",EDGE,{"disambiguationData":[TD([[subQ2,1.0]])],"derivedFrom":subQ1}),-1.0]])]});}
            var Q13;
            {var subQ0=sQuery(id+"F10.wireOp",EDGE,"E17");var subQ1=sQuery(id+"F10.wireOp",EDGE,"E14");var subQ2=makeQuery(id+"F10.imprint","INTERSECT",VERTEX,{"derivedFrom":[subQ1,subQ0]});Q13=makeQuery(id+"F10.imprint","IMPRINT",FACE,{"disambiguationData":[TD([[makeQuery(id+"F10.imprint","IMPRINT",EDGE,{"disambiguationData":[TD([[subQ2,1.0]])],"derivedFrom":subQ1}),-1.0]])]});}
            var Q14;
            {var subQ0=sQuery(id+"F10.wireOp",EDGE,"E18.MirrorC");var subQ1=sQuery(id+"F10.wireOp",EDGE,"E14");var subQ2=makeQuery(id+"F10.imprint","INTERSECT",VERTEX,{"derivedFrom":[subQ1,subQ0]});Q14=makeQuery(id+"F10.imprint","IMPRINT",FACE,{"disambiguationData":[TD([[makeQuery(id+"F10.imprint","IMPRINT",EDGE,{"disambiguationData":[TD([[subQ2,-1.0]])],"derivedFrom":subQ1}),-1.0]])]});}
            var Q15;
            {var subQ0=sQuery(id+"F10.wireOp",EDGE,"E19.1.1");var subQ1=sQuery(id+"F10.wireOp",EDGE,"E14");var subQ2=makeQuery(id+"F10.imprint","INTERSECT",VERTEX,{"derivedFrom":[subQ1,subQ0]});Q15=makeQuery(id+"F10.imprint","IMPRINT",FACE,{"disambiguationData":[TD([[makeQuery(id+"F10.imprint","IMPRINT",EDGE,{"disambiguationData":[TD([[subQ2,-1.0]])],"derivedFrom":subQ1}),-1.0]])]});}
            var Q16;
            {var subQ0=sQuery(id+"F10.wireOp",EDGE,"E19.1.2");var subQ1=sQuery(id+"F10.wireOp",EDGE,"E14");var subQ2=makeQuery(id+"F10.imprint","INTERSECT",VERTEX,{"derivedFrom":[subQ1,subQ0]});Q16=makeQuery(id+"F10.imprint","IMPRINT",FACE,{"disambiguationData":[TD([[makeQuery(id+"F10.imprint","IMPRINT",EDGE,{"disambiguationData":[TD([[subQ2,1.0]])],"derivedFrom":subQ1}),-1.0]])]});}
            var Q17;
            {var subQ0=sQuery(id+"F10.wireOp",EDGE,"E19.2.1");var subQ1=sQuery(id+"F10.wireOp",EDGE,"E14");var subQ2=makeQuery(id+"F10.imprint","INTERSECT",VERTEX,{"derivedFrom":[subQ1,subQ0]});Q17=makeQuery(id+"F10.imprint","IMPRINT",FACE,{"disambiguationData":[TD([[makeQuery(id+"F10.imprint","IMPRINT",EDGE,{"disambiguationData":[TD([[subQ2,-1.0]])],"derivedFrom":subQ1}),-1.0]])]});}
            var Q18;
            {var subQ0=sQuery(id+"F10.wireOp",EDGE,"E19.2.2");var subQ1=sQuery(id+"F10.wireOp",EDGE,"E14");var subQ2=makeQuery(id+"F10.imprint","INTERSECT",VERTEX,{"derivedFrom":[subQ1,subQ0]});Q18=makeQuery(id+"F10.imprint","IMPRINT",FACE,{"disambiguationData":[TD([[makeQuery(id+"F10.imprint","IMPRINT",EDGE,{"disambiguationData":[TD([[subQ2,1.0]])],"derivedFrom":subQ1}),-1.0]])]});}
            extrude(context, id + "F11", {"entities" : qUnion([Q0, Q1, Q2, Q3, Q4, Q5, Q6, Q7, Q8, Q9, Q10, Q11, Q12, Q13, Q14, Q15, Q16, Q17, Q18]), "depth" : 3.17 * mm, "offsetDistance" : 25.4 * mm});
        }
        {
            var Q0;
            Q0=makeQuery(id+"F11.opExtrude","CAP_FACE",FACE,{"disambiguationData":[OSD([sQuery(id+"F10.wireOp",EDGE,"E14"),sQuery(id+"F10.wireOp",EDGE,"E16"),sQuery(id+"F10.wireOp",EDGE,"E17"),sQuery(id+"F10.wireOp",EDGE,"E18.MirrorC"),sQuery(id+"F10.wireOp",EDGE,"E19.1.0"),sQuery(id+"F10.wireOp",EDGE,"E19.1.1"),sQuery(id+"F10.wireOp",EDGE,"E19.1.2"),sQuery(id+"F10.wireOp",EDGE,"E19.2.0"),sQuery(id+"F10.wireOp",EDGE,"E19.2.1"),sQuery(id+"F10.wireOp",EDGE,"E19.2.2"),sQuery(id+"F10.wireOp",EDGE,"E19.3.0"),sQuery(id+"F10.wireOp",EDGE,"E19.3.1"),sQuery(id+"F10.wireOp",EDGE,"E19.3.2")])],"isStart":false});
            var sketch = newSketch(context, id + "F12", { "sketchPlane" : qUnion([Q0])});
            skCircle(sketch, "E20", {"center": v(0, 0) * mm, "radius": 1.59 * mm});
            skSolve(sketch);
        }
        {
            var Q0;
            Q0 = qSketchRegion(id + "F12", true);
            extrude(context, id + "F13", {"entities" : qUnion([Q0]), "operationType" : NewBodyOperationType.REMOVE, "oppositeDirection" : true, "depth" : 25.4 * mm, "offsetDistance" : 25.4 * mm});
        }
        {
            var Q0;
            Q0=makeQuery(id+"F11.opExtrude","CAP_FACE",FACE,{"disambiguationData":[OSD([sQuery(id+"F10.wireOp",EDGE,"E14"),sQuery(id+"F10.wireOp",EDGE,"E16"),sQuery(id+"F10.wireOp",EDGE,"E17"),sQuery(id+"F10.wireOp",EDGE,"E18.MirrorC"),sQuery(id+"F10.wireOp",EDGE,"E19.1.0"),sQuery(id+"F10.wireOp",EDGE,"E19.1.1"),sQuery(id+"F10.wireOp",EDGE,"E19.1.2"),sQuery(id+"F10.wireOp",EDGE,"E19.2.0"),sQuery(id+"F10.wireOp",EDGE,"E19.2.1"),sQuery(id+"F10.wireOp",EDGE,"E19.2.2"),sQuery(id+"F10.wireOp",EDGE,"E19.3.0"),sQuery(id+"F10.wireOp",EDGE,"E19.3.1"),sQuery(id+"F10.wireOp",EDGE,"E19.3.2")])],"isStart":false});
            var sketch = newSketch(context, id + "F14", { "sketchPlane" : qUnion([Q0])});
            skCircle(sketch, "E21", {"center": v(-26.04, 26.04) * mm, "radius": 8.23 * mm});
            skCircle(sketch, "E22", {"center": v(-26.04, 26.04) * mm, "radius": 2.3 * mm});
            skSolve(sketch);
        }
        {
            var Q0;
            Q0 = qSketchRegion(id + "F14", true);
            extrude(context, id + "F15", {"entities" : qUnion([Q0]), "depth" : 3.17 * mm / 2, "offsetDistance" : 25.4 * mm});
        }
        {
            var Q0;
            Q0=makeQuery(id+"F15.opExtrude","SWEPT_BODY",BODY,{"disambiguationData":[OSD([sQuery(id+"F14.wireOp",EDGE,"E21"),sQuery(id+"F14.wireOp",EDGE,"E22")])]});
            var Q1;
            Q1=makeQuery(id+"F9.opExtrude","CAP_EDGE",EDGE,{"disambiguationData":[OSD([sQuery(id+"F8.wireOp",EDGE,"E13")])],"isStart":false});
            circularPattern(context, id + "F16", {"entities" : qUnion([Q0]), "axis" : qUnion([Q1]), "angle" : 360 * degree, "instanceCount" : 4, "oppositeDirection" : true, "equalSpace" : true});
        }
        {
            var Q0;
            Q0=makeQuery(id+"F5.opExtrude","CAP_FACE",FACE,{"disambiguationData":[OSD([sQuery(id+"F4.wireOp",EDGE,"E10.bottom"),sQuery(id+"F4.wireOp",EDGE,"E10.top"),sQuery(id+"F4.wireOp",EDGE,"E10.left"),sQuery(id+"F4.wireOp",EDGE,"E10.right")])],"isStart":false});
            var sketch = newSketch(context, id + "F17", { "sketchPlane" : qUnion([Q0])});
            skLineSegment(sketch, "E23.bottom", {"start": v(19.75, 26.71) * mm, "end": v(32.74, 26.71) * mm});
            skLineSegment(sketch, "E23.top", {"start": v(19.75, 15.7) * mm, "end": v(32.74, 15.7) * mm});
            skLineSegment(sketch, "E23.left", {"start": v(19.75, 26.71) * mm, "end": v(19.75, 15.7) * mm});
            skLineSegment(sketch, "E23.right", {"start": v(32.74, 26.71) * mm, "end": v(32.74, 15.7) * mm});
            skArc(sketch, "E24", {"start": v(31.73, 30.7) * mm, "mid": v(26.2, 36.18) * mm, "end": v(20.76, 30.61) * mm});
            skPoint(sketch, "E24.centerSnap0", {"position": v(26.25, 26.71) * mm});
            skLineSegment(sketch, "E25", {"start": v(20.76, 30.61) * mm, "end": v(20.76, 26.71) * mm});
            skArc(sketch, "E26", {"start": v(29.77, 30.7) * mm, "mid": v(26.29, 34.22) * mm, "end": v(22.72, 30.78) * mm});
            skLineSegment(sketch, "E27", {"start": v(22.72, 30.78) * mm, "end": v(22.8, 26.71) * mm});
            skLineSegment(sketch, "E28.top", {"start": v(29.77, 28.9) * mm, "end": v(31.73, 28.9) * mm});
            skLineSegment(sketch, "E28.left", {"start": v(29.77, 30.7) * mm, "end": v(29.77, 28.9) * mm});
            skLineSegment(sketch, "E28.right", {"start": v(31.73, 30.7) * mm, "end": v(31.73, 28.9) * mm});
            skPoint(sketch, "E29.orphan", {"position": v(20.76, 30.78) * mm});
            skCircle(sketch, "E30", {"center": v(26.2, 22.35) * mm, "radius": 1.61 * mm});
            skLineSegment(sketch, "E31", {"start": v(25.11, 21.17) * mm, "end": v(24.57, 17.2) * mm});
            skLineSegment(sketch, "E32", {"start": v(24.57, 17.2) * mm, "end": v(28, 17.2) * mm});
            skLineSegment(sketch, "E33", {"start": v(28, 17.2) * mm, "end": v(27.24, 21.12) * mm});
            skSolve(sketch);
        }
        {
            var Q0;
            Q0 = qSketchRegion(id + "F17", true);
            extrude(context, id + "F18", {"entities" : qUnion([Q0]), "operationType" : NewBodyOperationType.REMOVE, "oppositeDirection" : true, "depth" : 0.25 * mm, "offsetDistance" : 25.4 * mm});
        }
    });
